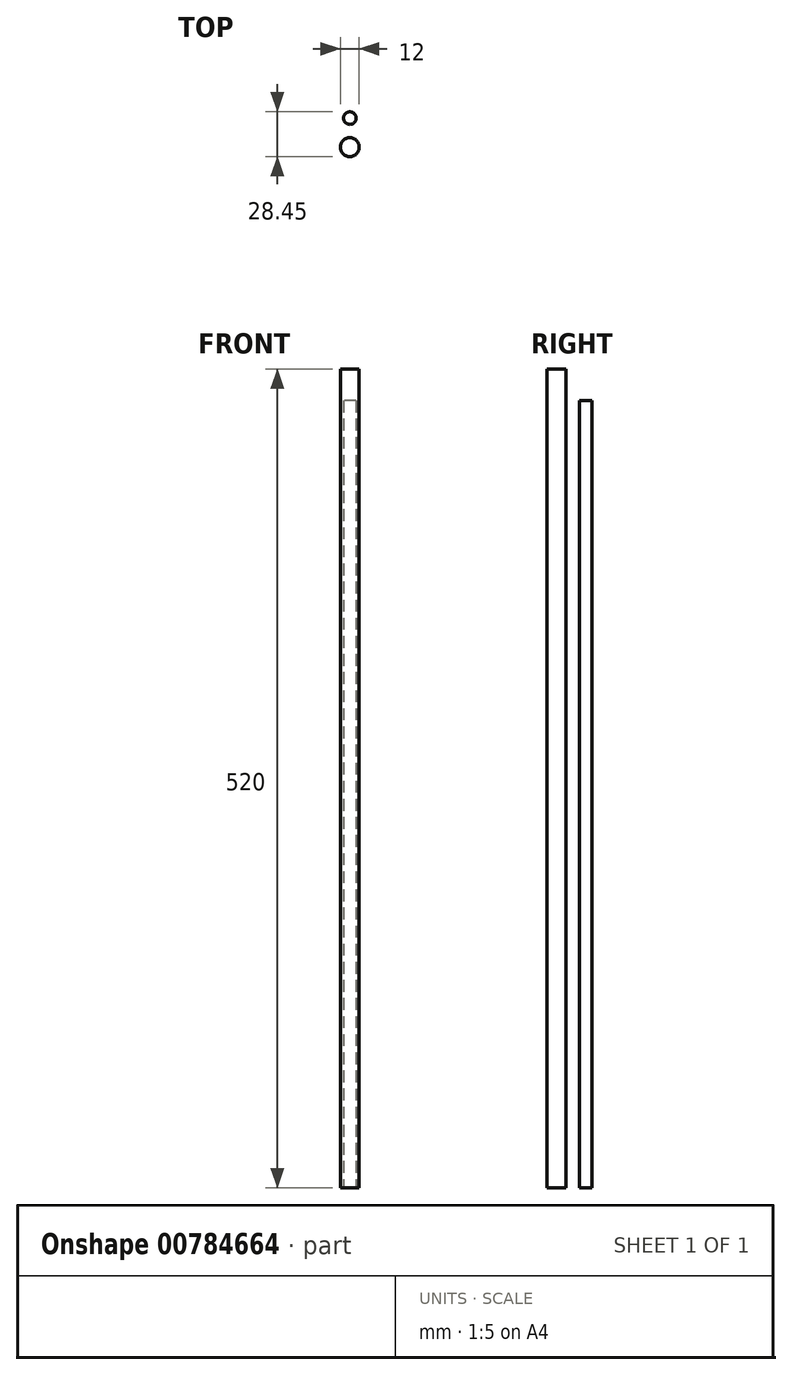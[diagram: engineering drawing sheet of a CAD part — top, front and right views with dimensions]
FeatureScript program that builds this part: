
annotation { "Feature Type Name" : "Feature", "Feature Type Description" : "" }
export const myFeature = defineFeature(function(context is Context, id is Id, definition is map)
    precondition{}
    {
        {
            var Q0;
            Q0=qCreatedBy(makeId("Top.planeOp"),FACE);
            var sketch = newSketch(context, id + "F0", { "sketchPlane" : qUnion([Q0])});
            skCircle(sketch, "E0", {"center": v(0, 0) * mm, "radius": 6 * mm});
            skCircle(sketch, "E1", {"center": v(0, 0) * mm, "radius": 4 * mm, "construction": true});
            skSolve(sketch);
        }
        {
            var Q0;
            Q0=qSketchRegion(id+"F0",true);
            extrude(context, id + "F1", {"entities" : qUnion([Q0]), "flatOperationType" : FlatOperationType.REMOVE, "offsetDistance" : 25 * mm, "depth" : 520 * mm, "domain" : OperationDomain.MODEL});
        }
        {
            var Q0;
            Q0=qCreatedBy(makeId("Top.planeOp"),FACE);
            var sketch = newSketch(context, id + "F2", { "sketchPlane" : qUnion([Q0]), "disableImprinting" : false});
            skCircle(sketch, "E2", {"center": v(0, 18.45) * mm, "radius": 4 * mm});
            skSolve(sketch);
        }
        {
            var Q0;
            Q0=makeQuery(id+"F2.imprint","IMPRINT",FACE,{"disambiguationData":[TD([[makeQuery(id+"F2.imprint","IMPRINT",EDGE,{"derivedFrom":sQuery(id+"F2.wireOp",EDGE,"E2")}),1.0]])]});
            extrude(context, id + "F3", {"entities" : qUnion([Q0]), "flatOperationType" : FlatOperationType.REMOVE, "offsetDistance" : 25 * mm, "depth" : 500 * mm, "domain" : OperationDomain.MODEL});
        }
    });
